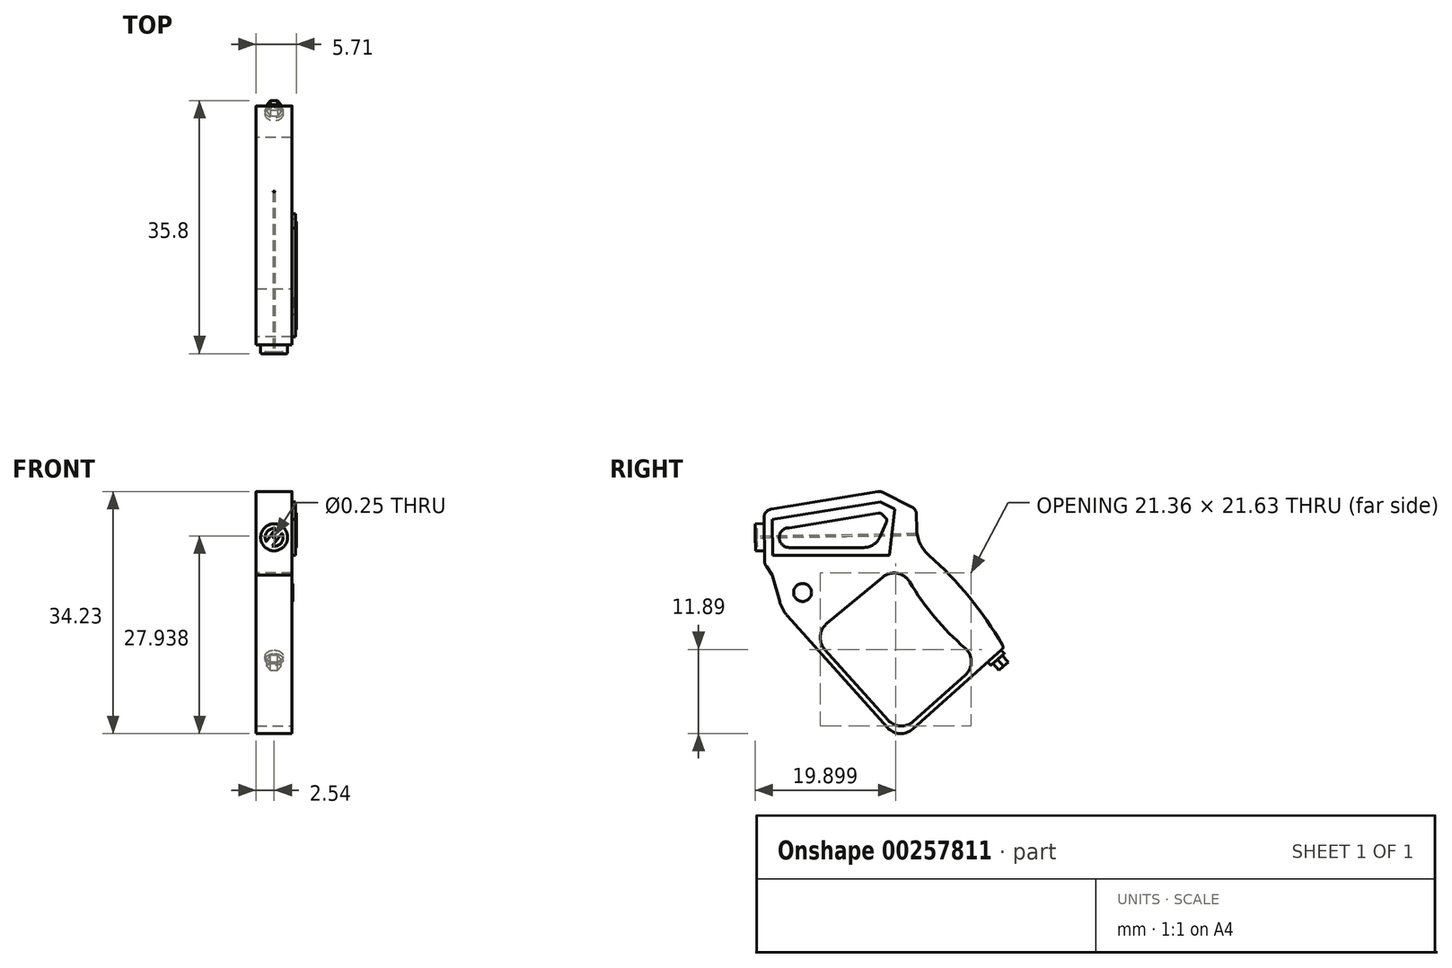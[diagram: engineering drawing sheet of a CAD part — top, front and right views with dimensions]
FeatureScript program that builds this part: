
annotation { "Feature Type Name" : "Feature", "Feature Type Description" : "" }
export const myFeature = defineFeature(function(context is Context, id is Id, definition is map)
    precondition{}
    {
        {
            var Q0;
            Q0=qCreatedBy(makeId("Right.planeOp"),FACE);
            var sketch = newSketch(context, id + "F0", { "sketchPlane" : qUnion([Q0])});
            skLineSegment(sketch, "E0.left", {"start": v(-13.65, 2.04) * mm, "end": v(-13.53, -5.58) * mm});
            skLineSegment(sketch, "E1", {"start": v(-13.65, 2.04) * mm, "end": v(2.86, 4.73) * mm});
            skLineSegment(sketch, "E2", {"start": v(7.94, 2.19) * mm, "end": v(2.86, 4.73) * mm});
            skLineSegment(sketch, "E3", {"start": v(17.66, -19.8) * mm, "end": v(20.31, -17.42) * mm});
            skLineSegment(sketch, "E4", {"start": v(7.94, 2.19) * mm, "end": v(8, -2.9) * mm});
            skLineSegment(sketch, "E5", {"start": v(-13.53, -5.58) * mm, "end": v(5.52, -5.45) * mm});
            skArc(sketch, "E6", {"start": v(20.31, -17.42) * mm, "mid": v(14.84, -9.57) * mm, "end": v(8, -2.9) * mm});
            skLineSegment(sketch, "E7", {"start": v(17.66, -19.8) * mm, "end": v(5.52, -30.6) * mm});
            skArc(sketch, "E8", {"start": v(5.52, -5.45) * mm, "mid": v(10.47, -13.06) * mm, "end": v(17.09, -19.28) * mm});
            skLineSegment(sketch, "E9", {"start": v(-13.53, -5.58) * mm, "end": v(-12.46, -7.16) * mm});
            skLineSegment(sketch, "E10", {"start": v(-12.46, -7.16) * mm, "end": v(-11.08, -12.04) * mm});
            skLineSegment(sketch, "E11", {"start": v(-11.08, -12.04) * mm, "end": v(5.52, -30.6) * mm});
            skLineSegment(sketch, "E12", {"start": v(5.52, -5.45) * mm, "end": v(-6.78, -15.7) * mm});
            skLineSegment(sketch, "E13", {"start": v(-6.78, -15.7) * mm, "end": v(5.58, -29.52) * mm});
            skLineSegment(sketch, "E14", {"start": v(5.58, -29.52) * mm, "end": v(17.09, -19.28) * mm});
            skSolve(sketch);
        }
        {
            var Q0;
            Q0=makeQuery(id+"F0.imprint","IMPRINT",FACE,{"disambiguationData":[TD([[makeQuery(id+"F0.imprint","IMPRINT",EDGE,{"derivedFrom":sQuery(id+"F0.wireOp",EDGE,"E0.left")}),1.0]])]});
            extrude(context, id + "F1", {"entities" : qUnion([Q0]), "depth" : 5.08 * mm});
        }
        {
            var Q0;
            Q0=makeQuery(id+"F1.opExtrude","SWEPT_FACE",FACE,{"disambiguationData":[OSD([sQuery(id+"F0.wireOp",EDGE,"E0.left")])]});
            var sketch = newSketch(context, id + "F2", { "sketchPlane" : qUnion([Q0])});
            skCircle(sketch, "E15", {"center": v(2.54, -1.56) * mm, "radius": 1.9 * mm});
            skCircle(sketch, "E16", {"center": v(2.54, -1.56) * mm, "radius": 1.27 * mm});
            skLineSegment(sketch, "E17", {"start": v(1.4, -2.13) * mm, "end": v(2.79, -0.31) * mm});
            skLineSegment(sketch, "E18", {"start": v(2.3, -2.8) * mm, "end": v(3.67, -0.98) * mm});
            skSolve(sketch);
        }
        {
            var Q0;
            Q0=makeQuery(id+"F2.imprint","IMPRINT",FACE,{"disambiguationData":[TD([[makeQuery(id+"F2.imprint","IMPRINT",EDGE,{"derivedFrom":sQuery(id+"F2.wireOp",EDGE,"E15")}),1.0]])]});
            var Q1;
            {var subQ0=sQuery(id+"F2.wireOp",EDGE,"E17");Q1=makeQuery(id+"F2.imprint","IMPRINT",FACE,{"disambiguationData":[TD([[makeQuery(id+"F2.imprint","IMPRINT",EDGE,{"derivedFrom":subQ0}),-1.0]])]});}
            extrude(context, id + "F3", {"entities" : qUnion([Q0, Q1]), "operationType" : NewBodyOperationType.ADD, "depth" : 1.27 * mm});
        }
        {
            var Q0;
            {var subQ0=sQuery(id+"F2.wireOp",EDGE,"E17");Q0=makeQuery(id+"F3.boolean.opBoolean","SPLIT",FACE,{"disambiguationData":[TD([makeQuery(id+"F3.opExtrude","SWEPT_FACE",FACE,{"disambiguationData":[OSD([subQ0])]})])],"derivedFrom":makeQuery(id+"F1.opExtrude","SWEPT_FACE",FACE,{"disambiguationData":[OSD([sQuery(id+"F0.wireOp",EDGE,"E0.left")])]})});}
            var Q1;
            {var subQ0=sQuery(id+"F2.wireOp",EDGE,"E18");Q1=makeQuery(id+"F3.boolean.opBoolean","SPLIT",FACE,{"disambiguationData":[TD([makeQuery(id+"F3.opExtrude","SWEPT_FACE",FACE,{"disambiguationData":[OSD([subQ0])]})])],"derivedFrom":makeQuery(id+"F1.opExtrude","SWEPT_FACE",FACE,{"disambiguationData":[OSD([sQuery(id+"F0.wireOp",EDGE,"E0.left")])]})});}
            extrude(context, id + "F4", {"entities" : qUnion([Q0, Q1]), "operationType" : NewBodyOperationType.ADD, "depth" : 1.02 * mm});
        }
        {
            var Q0;
            Q0=makeQuery(id+"F3.opExtrude","CAP_FACE",FACE,{"disambiguationData":[OSD([sQuery(id+"F2.wireOp",EDGE,"E15"),sQuery(id+"F2.wireOp",EDGE,"E16"),sQuery(id+"F2.wireOp",EDGE,"E17"),sQuery(id+"F2.wireOp",EDGE,"E18")])],"isStart":false});
            var sketch = newSketch(context, id + "F5", { "sketchPlane" : qUnion([Q0])});
            skCircle(sketch, "E19", {"center": v(2.54, -1.56) * mm, "radius": 0.13 * mm});
            skSolve(sketch);
        }
        {
            var Q0;
            Q0=sQuery(id+"F5.wireOp",VERTEX,"E19.center");
            var Q1;
            Q1=makeQuery(id+"F1.opExtrude","SWEPT_BODY",BODY,{"disambiguationData":[OSD([sQuery(id+"F0.wireOp",EDGE,"E0.left"),sQuery(id+"F0.wireOp",EDGE,"E1"),sQuery(id+"F0.wireOp",EDGE,"E2"),sQuery(id+"F0.wireOp",EDGE,"E3"),sQuery(id+"F0.wireOp",EDGE,"E4"),sQuery(id+"F0.wireOp",EDGE,"E6"),sQuery(id+"F0.wireOp",EDGE,"E7"),sQuery(id+"F0.wireOp",EDGE,"E8"),sQuery(id+"F0.wireOp",EDGE,"E9"),sQuery(id+"F0.wireOp",EDGE,"E10"),sQuery(id+"F0.wireOp",EDGE,"E11"),sQuery(id+"F0.wireOp",EDGE,"E12"),sQuery(id+"F0.wireOp",EDGE,"E13"),sQuery(id+"F0.wireOp",EDGE,"E14")])]});
            hole(context, id + "F6", {"style" : HoleStyle.SIMPLE, "endStyle" : HoleEndStyle.THROUGH, "holeDiameter" : 0.25 * mm, "tappedDepth" : 12.7 * mm, "tapClearance" : 3, "locations" : qUnion([Q0]), "scope" : qUnion([Q1])});
        }
        {
            var Q0;
            Q0=makeQuery(id+"F1.opExtrude","SWEPT_FACE",FACE,{"disambiguationData":[OSD([sQuery(id+"F0.wireOp",EDGE,"E3")])]});
            var sketch = newSketch(context, id + "F7", { "sketchPlane" : qUnion([Q0])});
            skCircle(sketch, "E20", {"center": v(2.54, -1.75) * mm, "radius": 1.27 * mm});
            skPoint(sketch, "E20.centerSnap0", {"position": v(2.54, -3.53) * mm});
            skSolve(sketch);
        }
        {
            var Q0;
            Q0=makeQuery(id+"F7.imprint","IMPRINT",FACE,{"disambiguationData":[TD([[makeQuery(id+"F7.imprint","IMPRINT",EDGE,{"derivedFrom":sQuery(id+"F7.wireOp",EDGE,"E20")}),1.0]])]});
            extrude(context, id + "F8", {"entities" : qUnion([Q0]), "operationType" : NewBodyOperationType.ADD, "depth" : 0.64 * mm});
        }
        {
            var Q0;
            Q0=makeQuery(id+"F8.opExtrude","CAP_FACE",FACE,{"disambiguationData":[OSD([sQuery(id+"F7.wireOp",EDGE,"E20")])],"isStart":false});
            var sketch = newSketch(context, id + "F9", { "sketchPlane" : qUnion([Q0])});
            skCircle(sketch, "E21", {"center": v(2.54, -1.75) * mm, "radius": 1.02 * mm});
            skLineSegment(sketch, "E22", {"start": v(3.56, -1.75) * mm, "end": v(3.05, -0.87) * mm});
            skLineSegment(sketch, "E23", {"start": v(1.52, -1.75) * mm, "end": v(2.03, -0.87) * mm});
            skLineSegment(sketch, "E24", {"start": v(3.56, -1.75) * mm, "end": v(3.05, -2.63) * mm});
            skLineSegment(sketch, "E25", {"start": v(1.52, -1.75) * mm, "end": v(2.03, -2.63) * mm});
            skLineSegment(sketch, "E26", {"start": v(2.03, -0.87) * mm, "end": v(3.05, -0.87) * mm});
            skLineSegment(sketch, "E27", {"start": v(3.05, -2.63) * mm, "end": v(2.03, -2.63) * mm});
            skSolve(sketch);
        }
        {
            var Q0;
            Q0=makeQuery(id+"F9.imprint","IMPRINT",FACE,{"disambiguationData":[TD([[makeQuery(id+"F9.imprint","IMPRINT",EDGE,{"derivedFrom":sQuery(id+"F9.wireOp",EDGE,"E22")}),1.0]])]});
            extrude(context, id + "F10", {"entities" : qUnion([Q0]), "operationType" : NewBodyOperationType.ADD, "depth" : 1.27 * mm});
        }
        {
            var Q0;
            Q0=makeQuery(id+"F1.opExtrude","CAP_FACE",FACE,{"disambiguationData":[OSD([sQuery(id+"F0.wireOp",EDGE,"E0.left"),sQuery(id+"F0.wireOp",EDGE,"E1"),sQuery(id+"F0.wireOp",EDGE,"E2"),sQuery(id+"F0.wireOp",EDGE,"E3"),sQuery(id+"F0.wireOp",EDGE,"E4"),sQuery(id+"F0.wireOp",EDGE,"E6"),sQuery(id+"F0.wireOp",EDGE,"E7"),sQuery(id+"F0.wireOp",EDGE,"E8"),sQuery(id+"F0.wireOp",EDGE,"E9"),sQuery(id+"F0.wireOp",EDGE,"E10"),sQuery(id+"F0.wireOp",EDGE,"E11"),sQuery(id+"F0.wireOp",EDGE,"E12"),sQuery(id+"F0.wireOp",EDGE,"E13"),sQuery(id+"F0.wireOp",EDGE,"E14")])],"isStart":false});
            var sketch = newSketch(context, id + "F11", { "sketchPlane" : qUnion([Q0])});
            skLineSegment(sketch, "E28", {"start": v(-12.47, 0.7) * mm, "end": v(-12.4, -4.37) * mm});
            skLineSegment(sketch, "E29", {"start": v(-12.47, 0.7) * mm, "end": v(2.86, 3.2) * mm});
            skLineSegment(sketch, "E30", {"start": v(2.86, 3.2) * mm, "end": v(4.89, 2.19) * mm});
            skLineSegment(sketch, "E31", {"start": v(4.89, 2.19) * mm, "end": v(4.12, -4.37) * mm});
            skLineSegment(sketch, "E32", {"start": v(-12.4, -4.37) * mm, "end": v(4.12, -4.37) * mm});
            skSolve(sketch);
        }
        {
            var Q0;
            Q0=makeQuery(id+"F11.imprint","IMPRINT",FACE,{"disambiguationData":[TD([[makeQuery(id+"F11.imprint","IMPRINT",EDGE,{"derivedFrom":sQuery(id+"F11.wireOp",EDGE,"E28")}),1.0]])]});
            extrude(context, id + "F12", {"entities" : qUnion([Q0]), "operationType" : NewBodyOperationType.ADD, "depth" : 0.5 * mm});
        }
        {
            var Q0;
            Q0=makeQuery(id+"F12.opExtrude","CAP_FACE",FACE,{"disambiguationData":[OSD([sQuery(id+"F11.wireOp",EDGE,"E28"),sQuery(id+"F11.wireOp",EDGE,"E29"),sQuery(id+"F11.wireOp",EDGE,"E30"),sQuery(id+"F11.wireOp",EDGE,"E31"),sQuery(id+"F11.wireOp",EDGE,"E32")])],"isStart":false});
            var sketch = newSketch(context, id + "F13", { "sketchPlane" : qUnion([Q0])});
            skLineSegment(sketch, "E33", {"start": v(-10.08, -0.44) * mm, "end": v(2.86, 1.67) * mm});
            skLineSegment(sketch, "E34", {"start": v(2.86, 1.67) * mm, "end": v(3.87, 0.7) * mm});
            skPoint(sketch, "E34.endSnap0", {"position": v(3.87, 2.7) * mm});
            skLineSegment(sketch, "E35", {"start": v(3.87, 0.7) * mm, "end": v(2.11, -3.23) * mm});
            skLineSegment(sketch, "E36", {"start": v(2.11, -3.23) * mm, "end": v(-10.08, -3.23) * mm});
            skArc(sketch, "E37", {"start": v(-10.08, -0.44) * mm, "mid": v(-11.48, -1.84) * mm, "end": v(-10.08, -3.23) * mm});
            skSolve(sketch);
        }
        {
            var Q0;
            Q0=makeQuery(id+"F13.imprint","IMPRINT",FACE,{"disambiguationData":[TD([[makeQuery(id+"F13.imprint","IMPRINT",EDGE,{"derivedFrom":sQuery(id+"F13.wireOp",EDGE,"E33")}),-1.0]])]});
            extrude(context, id + "F14", {"entities" : qUnion([Q0]), "operationType" : NewBodyOperationType.ADD, "depth" : 0.13 * mm});
        }
        {
            var Q0;
            Q0=makeQuery(id+"F1.opExtrude","CAP_FACE",FACE,{"disambiguationData":[OSD([sQuery(id+"F0.wireOp",EDGE,"E0.left"),sQuery(id+"F0.wireOp",EDGE,"E1"),sQuery(id+"F0.wireOp",EDGE,"E2"),sQuery(id+"F0.wireOp",EDGE,"E3"),sQuery(id+"F0.wireOp",EDGE,"E4"),sQuery(id+"F0.wireOp",EDGE,"E6"),sQuery(id+"F0.wireOp",EDGE,"E7"),sQuery(id+"F0.wireOp",EDGE,"E8"),sQuery(id+"F0.wireOp",EDGE,"E9"),sQuery(id+"F0.wireOp",EDGE,"E10"),sQuery(id+"F0.wireOp",EDGE,"E11"),sQuery(id+"F0.wireOp",EDGE,"E12"),sQuery(id+"F0.wireOp",EDGE,"E13"),sQuery(id+"F0.wireOp",EDGE,"E14")])],"isStart":false});
            var sketch = newSketch(context, id + "F15", { "sketchPlane" : qUnion([Q0])});
            skCircle(sketch, "E38", {"center": v(-8.18, -9.6) * mm, "radius": 1.27 * mm});
            skPoint(sketch, "E38.centerSnap0", {"position": v(-11.77, -9.6) * mm});
            skSolve(sketch);
        }
        {
            var Q0;
            Q0=makeQuery(id+"F15.imprint","IMPRINT",FACE,{"disambiguationData":[TD([[makeQuery(id+"F15.imprint","IMPRINT",EDGE,{"derivedFrom":sQuery(id+"F15.wireOp",EDGE,"E38")}),1.0]])]});
            extrude(context, id + "F16", {"entities" : qUnion([Q0]), "operationType" : NewBodyOperationType.ADD, "depth" : 0.13 * mm});
        }
        {
            var Q0;
            Q0=makeQuery(id+"F1.opExtrude","SWEPT_EDGE",EDGE,{"disambiguationData":[OSD([sQuery(id+"F0.wireOp",EDGE,"E8"),sQuery(id+"F0.wireOp",EDGE,"E12")])]});
            fillet(context, id + "F17", {"entities" : qUnion([Q0]), "radius" : 2.54 * mm, "tangentPropagation" : true, "allowEdgeOverflow" : false});
        }
        {
            var Q0;
            Q0=makeQuery(id+"F1.opExtrude","SWEPT_EDGE",EDGE,{"disambiguationData":[OSD([sQuery(id+"F0.wireOp",EDGE,"E8"),sQuery(id+"F0.wireOp",EDGE,"E14")])]});
            var Q1;
            Q1=makeQuery(id+"F1.opExtrude","SWEPT_EDGE",EDGE,{"disambiguationData":[OSD([sQuery(id+"F0.wireOp",EDGE,"E12"),sQuery(id+"F0.wireOp",EDGE,"E13")])]});
            fillet(context, id + "F18", {"entities" : qUnion([Q0, Q1]), "radius" : 2.54 * mm, "tangentPropagation" : true, "allowEdgeOverflow" : false});
        }
        {
            var Q0;
            Q0=makeQuery(id+"F1.opExtrude","SWEPT_EDGE",EDGE,{"disambiguationData":[OSD([sQuery(id+"F0.wireOp",EDGE,"E13"),sQuery(id+"F0.wireOp",EDGE,"E14")])]});
            fillet(context, id + "F19", {"entities" : qUnion([Q0]), "radius" : 2.54 * mm, "tangentPropagation" : true, "allowEdgeOverflow" : false});
        }
        {
            var Q0;
            Q0=makeQuery(id+"F1.opExtrude","SWEPT_EDGE",EDGE,{"disambiguationData":[OSD([sQuery(id+"F0.wireOp",EDGE,"E4"),sQuery(id+"F0.wireOp",EDGE,"E6")])]});
            fillet(context, id + "F20", {"entities" : qUnion([Q0]), "radius" : 5.08 * mm, "tangentPropagation" : true, "allowEdgeOverflow" : false});
        }
        {
            var Q0;
            Q0=makeQuery(id+"F1.opExtrude","SWEPT_EDGE",EDGE,{"disambiguationData":[OSD([sQuery(id+"F0.wireOp",EDGE,"E2"),sQuery(id+"F0.wireOp",EDGE,"E4")])]});
            var Q1;
            Q1=makeQuery(id+"F1.opExtrude","SWEPT_EDGE",EDGE,{"disambiguationData":[OSD([sQuery(id+"F0.wireOp",EDGE,"E1"),sQuery(id+"F0.wireOp",EDGE,"E2")])]});
            fillet(context, id + "F21", {"entities" : qUnion([Q0, Q1]), "radius" : 1.27 * mm, "tangentPropagation" : true, "allowEdgeOverflow" : false});
        }
        {
            var Q0;
            Q0=makeQuery(id+"F1.opExtrude","SWEPT_EDGE",EDGE,{"disambiguationData":[OSD([sQuery(id+"F0.wireOp",EDGE,"E0.left"),sQuery(id+"F0.wireOp",EDGE,"E1")])]});
            var Q1;
            Q1=makeQuery(id+"F1.opExtrude","SWEPT_EDGE",EDGE,{"disambiguationData":[OSD([sQuery(id+"F0.wireOp",EDGE,"E0.left"),sQuery(id+"F0.wireOp",EDGE,"E9")])]});
            fillet(context, id + "F22", {"entities" : qUnion([Q0, Q1]), "radius" : 1.27 * mm, "tangentPropagation" : true, "allowEdgeOverflow" : false});
        }
        {
            var Q0;
            Q0=makeQuery(id+"F1.opExtrude","SWEPT_EDGE",EDGE,{"disambiguationData":[OSD([sQuery(id+"F0.wireOp",EDGE,"E10"),sQuery(id+"F0.wireOp",EDGE,"E11")])]});
            fillet(context, id + "F23", {"entities" : qUnion([Q0]), "radius" : 5.08 * mm, "tangentPropagation" : true, "allowEdgeOverflow" : false});
        }
        {
            var Q0;
            Q0=makeQuery(id+"F1.opExtrude","SWEPT_EDGE",EDGE,{"disambiguationData":[OSD([sQuery(id+"F0.wireOp",EDGE,"E7"),sQuery(id+"F0.wireOp",EDGE,"E11")])]});
            fillet(context, id + "F24", {"entities" : qUnion([Q0]), "radius" : 2.54 * mm, "tangentPropagation" : true, "allowEdgeOverflow" : false});
        }
        {
            var Q0;
            Q0=makeQuery(id+"F1.opExtrude","SWEPT_EDGE",EDGE,{"disambiguationData":[OSD([sQuery(id+"F0.wireOp",EDGE,"E3"),sQuery(id+"F0.wireOp",EDGE,"E6")])]});
            fillet(context, id + "F25", {"entities" : qUnion([Q0]), "radius" : 0.5 * mm, "tangentPropagation" : true, "allowEdgeOverflow" : false});
        }
        {
            var Q0;
            Q0=makeQuery(id+"F14.opExtrude","SWEPT_EDGE",EDGE,{"disambiguationData":[OSD([sQuery(id+"F13.wireOp",EDGE,"E35"),sQuery(id+"F13.wireOp",EDGE,"E36")])]});
            fillet(context, id + "F26", {"entities" : qUnion([Q0]), "radius" : 2.54 * mm, "tangentPropagation" : true, "allowEdgeOverflow" : false});
        }
        {
            var Q0;
            Q0=makeQuery(id+"F14.opExtrude","SWEPT_EDGE",EDGE,{"disambiguationData":[OSD([sQuery(id+"F13.wireOp",EDGE,"E33"),sQuery(id+"F13.wireOp",EDGE,"E34")])]});
            fillet(context, id + "F27", {"entities" : qUnion([Q0]), "radius" : 0.64 * mm, "tangentPropagation" : true, "allowEdgeOverflow" : false});
        }
        {
            var Q0;
            Q0=makeQuery(id+"F14.opExtrude","SWEPT_EDGE",EDGE,{"disambiguationData":[OSD([sQuery(id+"F13.wireOp",EDGE,"E34"),sQuery(id+"F13.wireOp",EDGE,"E35")])]});
            fillet(context, id + "F28", {"entities" : qUnion([Q0]), "radius" : 0.64 * mm, "tangentPropagation" : true, "allowEdgeOverflow" : false});
        }
    });
